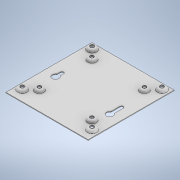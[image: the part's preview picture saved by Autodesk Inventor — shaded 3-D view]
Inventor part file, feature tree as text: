
AUTODESK INVENTOR PART (.ipt)
format: ipt  version: 2020 (Build 240168000, 168)  size: 317,952 bytes
history: native  units: mm
features: extrude x6, sketch x4, fillet x2
ambient origin geometry x8: Origin, YZ Plane, XZ Plane, XY Plane, X Axis, Y Axis, Z Axis, Center Point
bodies: Solid1 (feature_tree)
feature tree (12):
  extrude  "Extrusion1"  Depth=116.5mm
  extrude  "Extrusion2"  Depth=1.0mm
  extrude  "Extrusion3"  Depth=1.0mm
  extrude  "Extrusion7"  Depth=13.625mm
  fillet  "Fillet1"  Radius=4.6mm
  extrude  "Extrusion9"  Depth=13.625mm
  fillet  "Fillet3"  Radius=3.75mm
  extrude  "Extrusion10"  Depth=3.7mm
  sketch  "Sketch1"  dims[d0=121.9mm d1=116.5mm]
  sketch  "Sketch2"  dims[d2=1.0mm d3=0.0mm d5=13.2mm]
  sketch  "Sketch3"  dims[d6=1.0mm d7=0.0mm d8=8.4mm]
  sketch  "Sketch6"  dims[d27=1.0mm d28=0.0mm d53=20.0mm d55=74.5mm d56=20.0mm d58=74.5mm d70=4.6mm d71=20.0mm d73=74.5mm d74=20.0mm d76=74.5mm d79=3.75mm d80=0.0mm d81=3.7mm d83=4.6mm d86=20.0mm d88=99.0mm d89=20.0mm d91=99.0mm d99=3.75mm d100=0.0mm d101=3.7mm d103=21.0mm d104=21.0mm d105=20.0mm d107=74.5mm d108=20.0mm d110=74.5mm d116=4.75mm d117=16.0mm d118=56.0mm d119=14.0mm d120=13.625mm d121=13.625mm d122=21.5mm d123=9.5mm d124=9.5mm d125=0.0mm d126=0.0mm d127=8.1mm d128=20.0mm d130=99.0mm d131=20.0mm d133=99.0mm d136=13.2mm d137=20.0mm d139=99.0mm d140=20.0mm d142=99.0mm]
